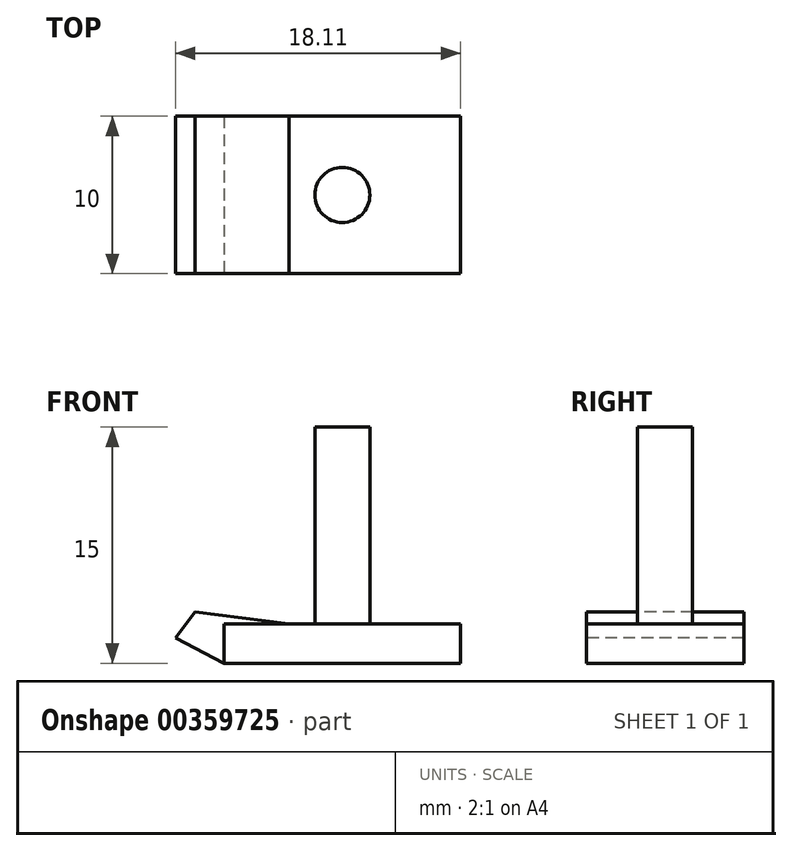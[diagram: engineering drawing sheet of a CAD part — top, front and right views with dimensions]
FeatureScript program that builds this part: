
annotation { "Feature Type Name" : "Feature", "Feature Type Description" : "" }
export const myFeature = defineFeature(function(context is Context, id is Id, definition is map)
    precondition{}
    {
        {
            var Q0;
            Q0=qCreatedBy(makeId("Top.planeOp"),FACE);
            var sketch = newSketch(context, id + "F0", { "sketchPlane" : qUnion([Q0])});
            skCircle(sketch, "E0", {"center": v(0, 0) * mm, "radius": 1.75 * mm});
            skLineSegment(sketch, "E1.bottom", {"start": v(7.5, 5) * mm, "end": v(-7.5, 5) * mm});
            skLineSegment(sketch, "E1.top", {"start": v(7.5, -5) * mm, "end": v(-7.5, -5) * mm});
            skLineSegment(sketch, "E1.left", {"start": v(7.5, 5) * mm, "end": v(7.5, -5) * mm});
            skLineSegment(sketch, "E1.right", {"start": v(-7.5, 5) * mm, "end": v(-7.5, -5) * mm});
            skSolve(sketch);
        }
        {
            var Q0;
            Q0=makeQuery(id+"F0.imprint","IMPRINT",FACE,{"disambiguationData":[TD([[makeQuery(id+"F0.imprint","IMPRINT",EDGE,{"derivedFrom":sQuery(id+"F0.wireOp",EDGE,"E0")}),1.0]])]});
            extrude(context, id + "F1", {"entities" : qUnion([Q0]), "depth" : 15 * mm});
        }
        {
            var Q0;
            Q0=makeQuery(id+"F0.imprint","IMPRINT",FACE,{"disambiguationData":[TD([[makeQuery(id+"F0.imprint","IMPRINT",EDGE,{"derivedFrom":sQuery(id+"F0.wireOp",EDGE,"E0")}),-1.0]])]});
            extrude(context, id + "F2", {"entities" : qUnion([Q0]), "operationType" : NewBodyOperationType.ADD, "depth" : 2.5 * mm});
        }
        {
            var Q0;
            Q0=makeQuery(id+"F2.opExtrude","SWEPT_FACE",FACE,{"disambiguationData":[OSD([sQuery(id+"F0.wireOp",EDGE,"E1.top")])]});
            var sketch = newSketch(context, id + "F3", { "sketchPlane" : qUnion([Q0])});
            skLineSegment(sketch, "E2", {"start": v(-7.5, 0) * mm, "end": v(-10.6, 1.61) * mm});
            skLineSegment(sketch, "E3", {"start": v(-7.5, 2.5) * mm, "end": v(-9.35, 3.27) * mm});
            skLineSegment(sketch, "E4", {"start": v(-10.6, 1.61) * mm, "end": v(-9.35, 3.27) * mm});
            skLineSegment(sketch, "E5", {"start": v(-9.35, 3.27) * mm, "end": v(-3.4, 2.5) * mm});
            skSolve(sketch);
        }
        {
            var Q0;
            Q0=makeQuery(id+"F3.imprint","IMPRINT",FACE,{"disambiguationData":[TD([[makeQuery(id+"F3.imprint","IMPRINT",EDGE,{"derivedFrom":sQuery(id+"F3.wireOp",EDGE,"E2")}),-1.0]])]});
            var Q1;
            {var subQ0=sQuery(id+"F3.wireOp",EDGE,"E3");Q1=makeQuery(id+"F3.imprint","IMPRINT",FACE,{"disambiguationData":[TD([[makeQuery(id+"F3.imprint","IMPRINT",EDGE,{"derivedFrom":subQ0}),-1.0]])]});}
            extrude(context, id + "F4", {"entities" : qUnion([Q0, Q1]), "oppositeDirection" : true, "depth" : 10 * mm});
        }
    });
